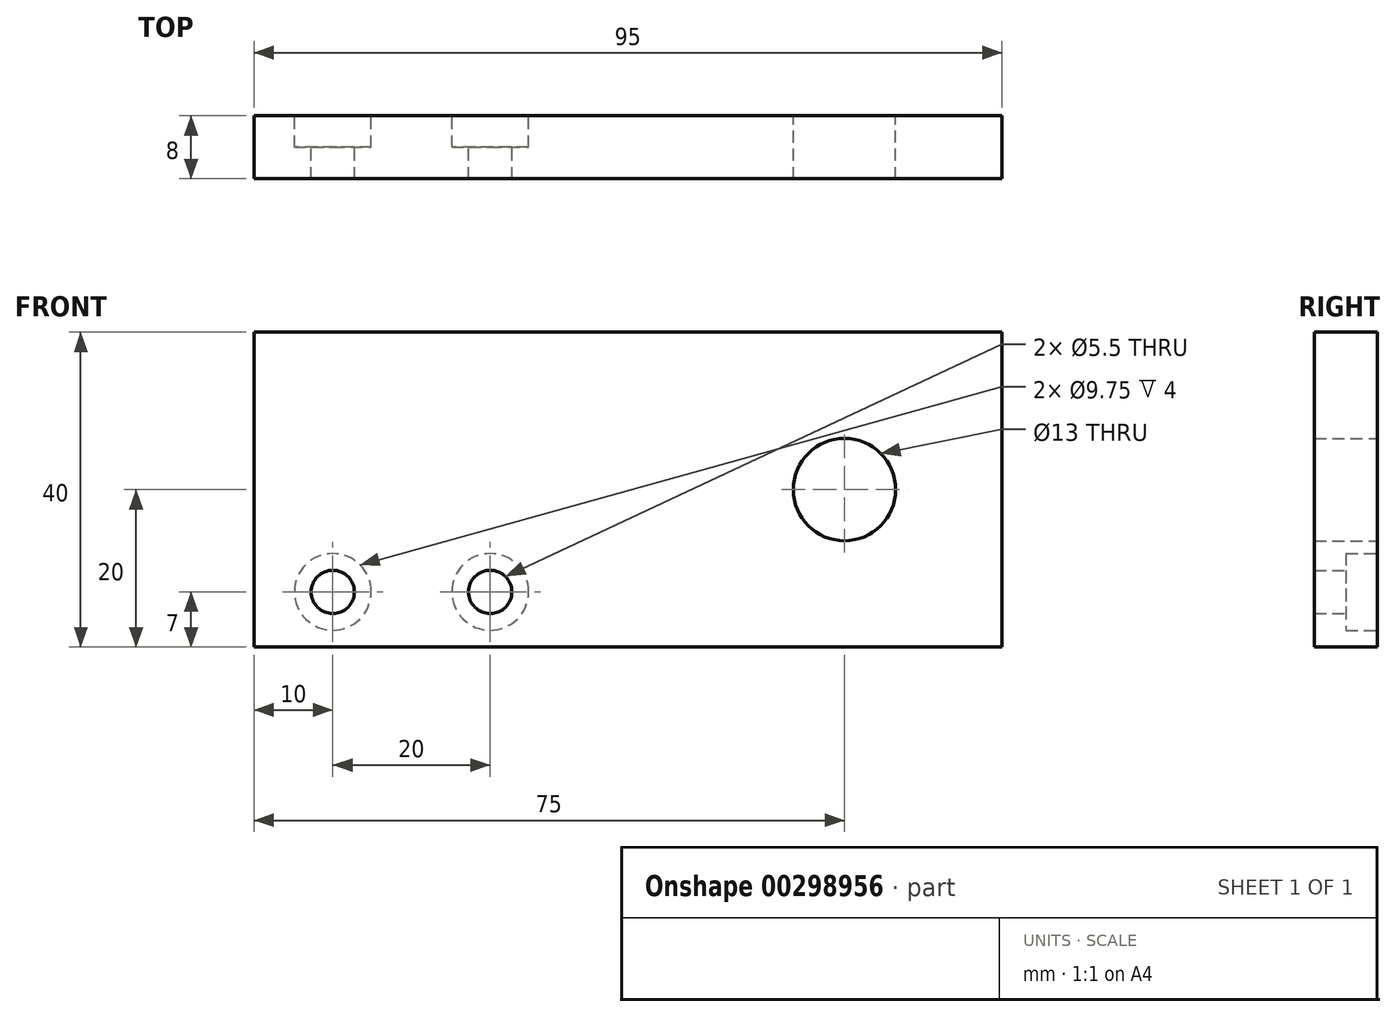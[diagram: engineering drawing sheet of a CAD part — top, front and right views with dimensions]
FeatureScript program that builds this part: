
annotation { "Feature Type Name" : "Feature", "Feature Type Description" : "" }
export const myFeature = defineFeature(function(context is Context, id is Id, definition is map)
    precondition{}
    {
        {
            var Q0;
            Q0=qCreatedBy(makeId("Front.planeOp"),FACE);
            var sketch = newSketch(context, id + "F0", { "sketchPlane" : qUnion([Q0])});
            skLineSegment(sketch, "E0.bottom", {"start": v(-47.5, 20) * mm, "end": v(47.5, 20) * mm});
            skLineSegment(sketch, "E0.top", {"start": v(-47.5, -20) * mm, "end": v(47.5, -20) * mm});
            skLineSegment(sketch, "E0.left", {"start": v(-47.5, 20) * mm, "end": v(-47.5, -20) * mm});
            skLineSegment(sketch, "E0.right", {"start": v(47.5, 20) * mm, "end": v(47.5, -20) * mm});
            skPoint(sketch, "E0.middle", {"position": v(0, 0) * mm});
            skPoint(sketch, "E1", {"position": v(-37.5, -13) * mm});
            skPoint(sketch, "E2", {"position": v(-17.5, -13) * mm});
            skPoint(sketch, "E3", {"position": v(27.5, 0) * mm});
            skSolve(sketch);
        }
        {
            var Q0;
            Q0=makeQuery(id+"F0.imprint","IMPRINT",FACE,{"disambiguationData":[TD([[makeQuery(id+"F0.imprint","IMPRINT",EDGE,{"derivedFrom":sQuery(id+"F0.wireOp",EDGE,"E0.bottom")}),-1.0]])]});
            extrude(context, id + "F1", {"entities" : qUnion([Q0]), "depth" : 8 * mm});
        }
        {
            var Q0;
            Q0=sQuery(id+"F0.wireOp",VERTEX,"E2");
            var Q1;
            Q1=sQuery(id+"F0.wireOp",VERTEX,"E1");
            var Q2;
            Q2=makeQuery(id+"F1.opExtrude","SWEPT_BODY",BODY,{"disambiguationData":[OSD([sQuery(id+"F0.wireOp",EDGE,"E0.bottom"),sQuery(id+"F0.wireOp",EDGE,"E0.top"),sQuery(id+"F0.wireOp",EDGE,"E0.left"),sQuery(id+"F0.wireOp",EDGE,"E0.right")])]});
            hole(context, id + "F2", {"style" : HoleStyle.C_BORE, "endStyle" : HoleEndStyle.THROUGH, "oppositeDirection" : true, "holeDiameter" : 5.5 * mm, "cBoreDiameter" : 9.75 * mm, "cBoreDepth" : 4 * mm, "isTappedThrough" : true, "tappedDepth" : 12 * mm, "tapClearance" : 3, "locations" : qUnion([Q0, Q1]), "scope" : qUnion([Q2])});
        }
        {
            var Q0;
            Q0=sQuery(id+"F0.wireOp",VERTEX,"E3");
            var Q1;
            Q1=makeQuery(id+"F1.opExtrude","SWEPT_BODY",BODY,{"disambiguationData":[OSD([sQuery(id+"F0.wireOp",EDGE,"E0.bottom"),sQuery(id+"F0.wireOp",EDGE,"E0.top"),sQuery(id+"F0.wireOp",EDGE,"E0.left"),sQuery(id+"F0.wireOp",EDGE,"E0.right")])]});
            hole(context, id + "F3", {"style" : HoleStyle.SIMPLE, "endStyle" : HoleEndStyle.THROUGH, "oppositeDirection" : true, "holeDiameter" : 13 * mm, "isTappedThrough" : true, "tappedDepth" : 12 * mm, "tapClearance" : 3, "locations" : qUnion([Q0]), "scope" : qUnion([Q1])});
        }
    });
